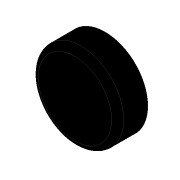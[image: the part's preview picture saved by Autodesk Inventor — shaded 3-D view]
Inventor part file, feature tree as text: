
AUTODESK INVENTOR PART (.ipt)
format: ipt  version: 2020 (Build 240168000, 168)  size: 102,912 bytes
history: native  units: mm
features: other x1, extrude x1, fillet x1, sketch x1
ambient origin geometry x8: Origin, YZ Plane, XZ Plane, XY Plane, X Axis, Y Axis, Z Axis, Center Point
bodies: Body1 (feature_tree)
feature tree (4):
  other  "솔리드1"
  extrude  "돌출1"  Depth=42.4mm
  fillet  "모깎기1"  Radius=15.0mm
  sketch  "스케치1"
